# Revit family: 54552207(2022)
name_source: partatom
category: Plumbing Fixtures
units: mm (PartAtom-declared; Revit-internal decimal feet)

## family parameters
Always vertical = Yes
Cut with Voids When Loaded = No
OmniClass Number = 23.45.55.00
OmniClass Title = Sanitary Faucets, Wastes
Part Type = Normal
Room Calculation Point = No
Round Connector Dimension = Use Diameter
Shared = No
Work Plane-Based = No

## types (1)
- 54552207 Washbasin faucet
    2D/3D/BIM Files URL = http://static.hansa.com
    3D View = https://static.hansa.com
    Advanced Features = Inner body made of DZR brass
    Aerator = Standard aerator;PCA® - constant flow rate regardless of pressure variations
    AssetType = Fixed
    BIMObjectName = 54552207(2022)
    Backflow Prevention EN1717 = AA
    BodyMaterial = Brass
    Brand = HANSA
    CO2 Emissions (A1-A3) = 9.4
    CO2 Emissions (A4) = 0.26
    CO2 Emissions (B7) = 1854
    CO2 Emissions (C2) = 0.02
    CO2 Emissions (C3) = 0.02
    CO2 Emissions (C4) = 0.07
    CO2 Emissions (D) = -6.68
    Catalog Drawing URL = http://static.hansa.com
    Category = Washbasin
    CloseOffRating = 0
    Color = Chrome
    Connection = Flexible inlet pipes
    Connection Size = G3/8
    Default Elevation = 0 mm  [stored 0 ft]
    Dimension Drawing URL = http://static.hansa.com
    DurationUnit = Year
    EAN Number = 4057304017452
    EN Standard = EN 817
    ETIM Class Number = EC011328 Washbasin mixing tap
    Excluded Items = Without pop-up waste
    FDV Document URL = http://www.hansa.com
    FaucetMainMaterial = Brass
    Features = Single-lever, side operated
    Finish = Polished
    Flow Drawing URL = http://static.hansa.com
    Flow Rate At 300kPa With Flow Controller = 0.0 L/s
    FlowCoefficient = 0
    Group = Washbasin faucet
    IfcExportAs = IfcValveType
    IfcExportType = FAUCET
    InletConnectionSize = 10 mm  [stored 0.0328084 ft]
    Installation Type = Deck mounted
    Installation and Maintenance Guide URL = http://static.hansa.com
    Interactive AR View URL = https://static.hansa.com
    Lever Handle = Single operating lever/handle;Pin shape;Hot/Cold symbols
    Manufacturer = HANSA
    ManufacturerName = HANSA
    ManufacturerURL = http://www.hansa.com
    Market = International;Germany;Austria;Belgium;Netherlands;Czech Republic;Slovakia;Italy
    Material = Brass
    Max. Hot Water Supply = 70 °C
    Mechanical Parts = 30Cartridge
    Mobile Product Information URL = http://mpi.hansa.com
    Model = 54552207 Washbasin faucet
    ModelReference = 54552207
    Mounting Holes = 1 hole
    NBSDescription = Water supply fittings for wash basins and troughs
    NBSReference = 45-35-70/371
    Name = 54552207 Washbasin faucet
    Name_en = 54552207 Washbasin faucet
    Noise Class = I (ISO 3822)
    NominalDepth = 183 mm
    NominalHeight = 239 mm
    NominalWidth = 99 mm
    Product Code = 54552207
    Product Family = HANSAVANTIS Style
    Product Image URL = http://static.hansa.com
    Product URL = http://static.hansa.com
    Sales Package dimensions (LxWxH) = 374 x 214 x 116
    Shape = Sculptured
    Size = 100x185x240 mm
    Spare-Part Information URL = http://static.hansa.com
    Spout Projection = 147 mm
    Spout Swivel Range = 120°
    Spout Type = Swivel spout
    Surface treatment = Chrome
    Technical DataSheet URL = http://www.hansa.com
    Temperature Adjustments = Limitation option for maximum temperature and flow-rate
    UNSPSC Class Number = 30181700 Faucets or taps
    URL Declaration Of Performance (DOP) = http://static.hansa.com
    URL Declaration of Asbestos = http://static.hansa.com
    URL Declaration of Conformity = http://static.hansa.com
    URL Declaration of SCIP = http://static.hansa.com
    URL EU Packaging Declaration = http://static.hansa.com
    URL EcoLabel Declaration = http://static.hansa.com
    URL Environmental Product Declaration EPD = http://www.hansa.com faucet.pdf
    URL Materials Declaration = http://www.hansa.com
    URL REACH = http://static.hansa.com
    URL UWL = http://static.hansa.com
    Uniclass2 = Pr_40_30_96_96
    Uniclass2015Description = Washbasin manual water supply sets
    Uniclass2015Reference = Pr_40_20_87_96
    Version = 1
    VersionDate = 01/06/2023
    Warranty Information URL = http://warranty.hansa.com
    WarrantyDescription = http://warranty.hansa.com
    WarrantyDurationUnit = Year
    Working Pressure = 50 - 1000 kPa

note: [stored X ft] marks values corroborated as IEEE doubles in the binary element streams (Revit-internal decimal feet)

## geometry (parser evidence)
native form markers: Sweep x5
no freeform markers — native parametric forms only
